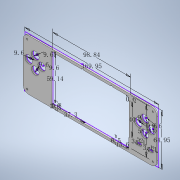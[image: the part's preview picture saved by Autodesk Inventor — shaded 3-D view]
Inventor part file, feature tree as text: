
AUTODESK INVENTOR PART (.ipt)
format: ipt  version: 2022 (Build 260153000, 153)  size: 315,392 bytes
history: native  units: mm
features: sketch x3, extrude x3, fillet x1, hole x1
ambient origin geometry x8: Origin, YZ Plane, XZ Plane, XY Plane, X Axis, Y Axis, Z Axis, Center Point
bodies: 实体3 (feature_tree)
feature tree (8):
  sketch  "草图1"  dims[d2=9.6mm d3=9.6mm d4=9.6mm d5=9.6mm d6=9.6mm d7=9.6mm d8=9.6mm d9=9.6mm d10=2.0mm d12=2.0mm]
  extrude  "拉伸3"  Depth=59.14mm
  extrude  "拉伸4"  Depth=0.8mm TaperAngle=0.0deg
  fillet  "圆角1"  Radius=0.8mm
  hole  "孔1"  [1 undecoded]
  extrude  "拉伸5"  Depth=0.8mm
  sketch  "草图2"  dims[d19=30.0mm d21=20.0mm d22=98.84mm d23=58.34mm d24=2.6mm d25=0.8mm d26=37.3mm d27=59.14mm d28=15.6mm d29=0.5mm d31=169.95mm]
  sketch  "草图3"  dims[d32=64.95mm d39=2.2mm d40=0.0mm d41=0.8mm d42=0.0mm d43=7.1mm d44=3.1mm d45=7.1mm d46=3.1mm d47=8.0mm d48=1.2mm d49=1.2mm d50=1.2mm d51=1.2mm d52=1.2mm d53=5.94614mm d54=2.0mm d55=2.0mm d56=90.0deg d57=4.0mm d58=0.0mm d59=34.5mm d60=64.95mm d61=0.7mm d62=0.0mm d64=40.0mm d65=0.6mm d63=0.5mm d66=0.872665mm]
note: 1 required parameter value undecoded (feature->parameter linkage not recoverable at this tier; creation-order binding heuristic only, values carry confidence <= 0.55)
